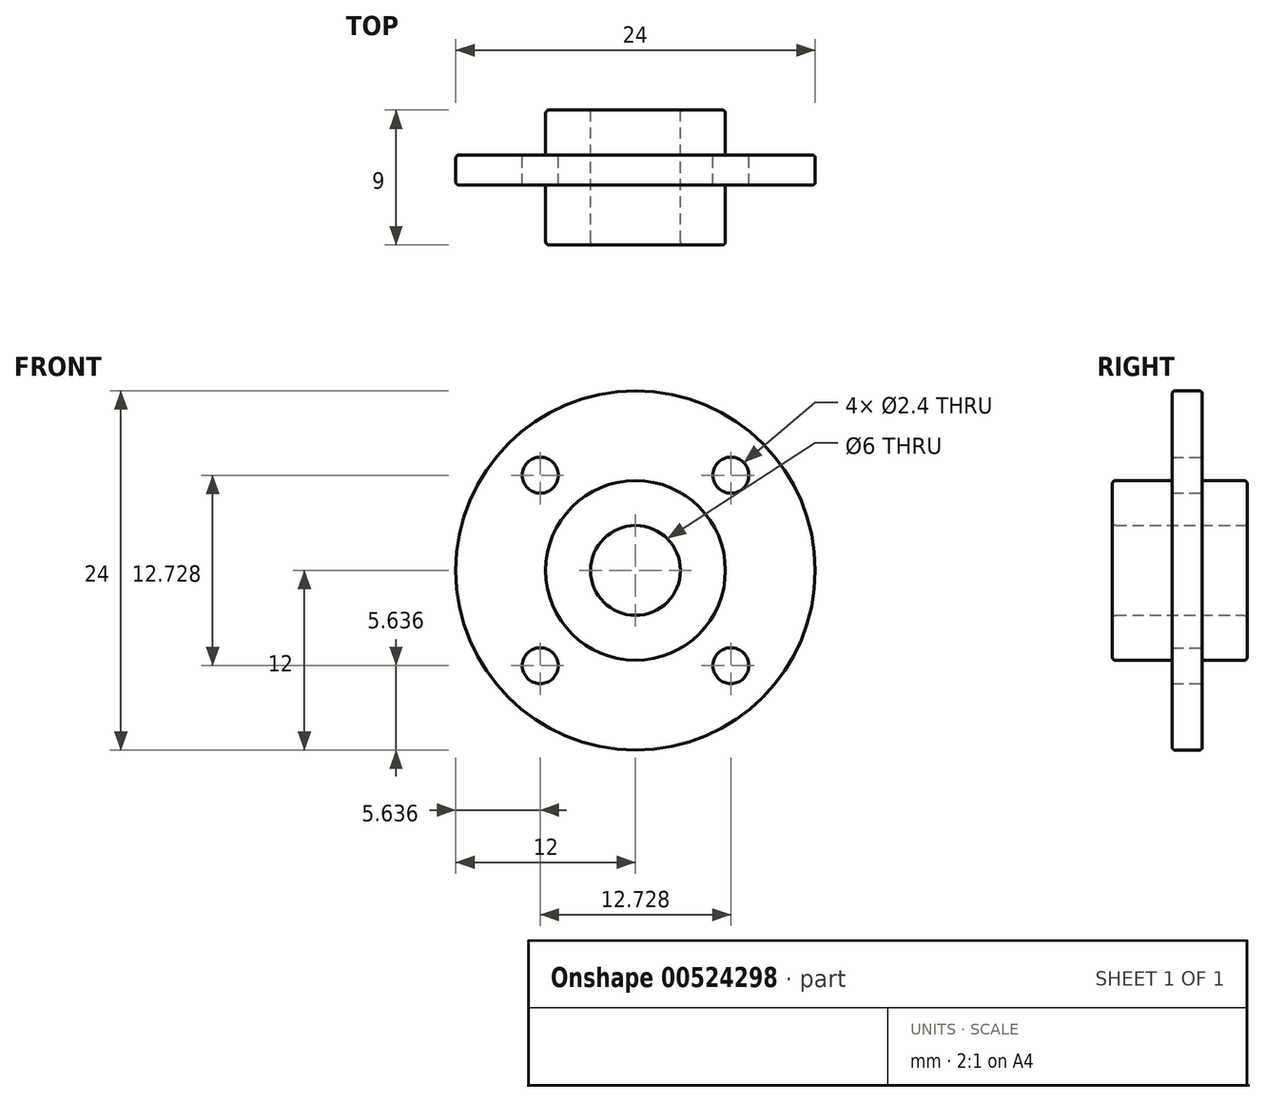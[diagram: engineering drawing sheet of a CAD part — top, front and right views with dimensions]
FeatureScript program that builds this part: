
annotation { "Feature Type Name" : "Feature", "Feature Type Description" : "" }
export const myFeature = defineFeature(function(context is Context, id is Id, definition is map)
    precondition{}
    {
        {
            var Q0;
            Q0=qCreatedBy(makeId("Front.planeOp"),FACE);
            var sketch = newSketch(context, id + "F0", { "sketchPlane" : qUnion([Q0])});
            skCircle(sketch, "E0", {"center": v(0, 0) * mm, "radius": 12 * mm});
            skCircle(sketch, "E1", {"center": v(0, 0) * mm, "radius": 9 * mm, "construction": true});
            skCircle(sketch, "E2", {"center": v(0, 0) * mm, "radius": 6 * mm});
            skCircle(sketch, "E3", {"center": v(0, 0) * mm, "radius": 3 * mm});
            skLineSegment(sketch, "E4", {"start": v(0, 12) * mm, "end": v(0, -12) * mm, "construction": true});
            skLineSegment(sketch, "E5", {"start": v(-12, 0) * mm, "end": v(12, 0) * mm, "construction": true});
            skLineSegment(sketch, "E6", {"start": v(-8.49, -8.49) * mm, "end": v(8.49, 8.49) * mm, "construction": true});
            skLineSegment(sketch, "E7", {"start": v(-8.49, 8.49) * mm, "end": v(8.49, -8.49) * mm, "construction": true});
            skCircle(sketch, "E8", {"center": v(-6.36, 6.36) * mm, "radius": 1.2 * mm});
            skCircle(sketch, "E9", {"center": v(6.36, 6.36) * mm, "radius": 1.2 * mm});
            skCircle(sketch, "E10", {"center": v(6.36, -6.36) * mm, "radius": 1.2 * mm});
            skCircle(sketch, "E11", {"center": v(-6.36, -6.36) * mm, "radius": 1.2 * mm});
            skSolve(sketch);
        }
        {
            var Q0;
            Q0=makeQuery(id+"F0.imprint","IMPRINT",FACE,{"disambiguationData":[TD([[makeQuery(id+"F0.imprint","IMPRINT",EDGE,{"derivedFrom":sQuery(id+"F0.wireOp",EDGE,"E0")}),1.0]])]});
            extrude(context, id + "F1", {"entities" : qUnion([Q0]), "depth" : 2 * mm, "offsetDistance" : 25 * mm});
        }
        {
            var Q0;
            Q0=makeQuery(id+"F0.imprint","IMPRINT",FACE,{"disambiguationData":[TD([[makeQuery(id+"F0.imprint","IMPRINT",EDGE,{"derivedFrom":sQuery(id+"F0.wireOp",EDGE,"E2")}),1.0]])]});
            extrude(context, id + "F2", {"entities" : qUnion([Q0]), "operationType" : NewBodyOperationType.ADD, "depth" : 6 * mm, "offsetDistance" : 25 * mm});
        }
        {
            var Q0;
            Q0=makeQuery(id+"F0.imprint","IMPRINT",FACE,{"disambiguationData":[TD([[makeQuery(id+"F0.imprint","IMPRINT",EDGE,{"derivedFrom":sQuery(id+"F0.wireOp",EDGE,"E2")}),1.0]])]});
            extrude(context, id + "F3", {"entities" : qUnion([Q0]), "operationType" : NewBodyOperationType.ADD, "oppositeDirection" : true, "depth" : 3 * mm, "offsetDistance" : 25 * mm});
        }
        {
            var Q0;
            Q0=makeQuery(id+"F2.opExtrude","CAP_EDGE",EDGE,{"disambiguationData":[OSD([sQuery(id+"F0.wireOp",EDGE,"E2")])],"isStart":false});
            var Q1;
            Q1=makeQuery(id+"F2.opExtrude","CAP_EDGE",EDGE,{"disambiguationData":[OSD([sQuery(id+"F0.wireOp",EDGE,"E3")])],"isStart":false});
            var Q2;
            Q2=makeQuery(id+"F1.opExtrude","CAP_EDGE",EDGE,{"disambiguationData":[OSD([sQuery(id+"F0.wireOp",EDGE,"E0")])],"isStart":false});
            var Q3;
            Q3=makeQuery(id+"F1.opExtrude","CAP_EDGE",EDGE,{"disambiguationData":[OSD([sQuery(id+"F0.wireOp",EDGE,"E0")])],"isStart":true});
            var Q4;
            Q4=makeQuery(id+"F3.opExtrude","CAP_EDGE",EDGE,{"disambiguationData":[OSD([sQuery(id+"F0.wireOp",EDGE,"E2")])],"isStart":false});
            var Q5;
            Q5=makeQuery(id+"F3.opExtrude","CAP_EDGE",EDGE,{"disambiguationData":[OSD([sQuery(id+"F0.wireOp",EDGE,"E3")])],"isStart":false});
            fillet(context, id + "F4", {"entities" : qUnion([Q0, Q1, Q2, Q3, Q4, Q5]), "radius" : 0.2 * mm, "tangentPropagation" : true, "allowEdgeOverflow" : false});
        }
    });
